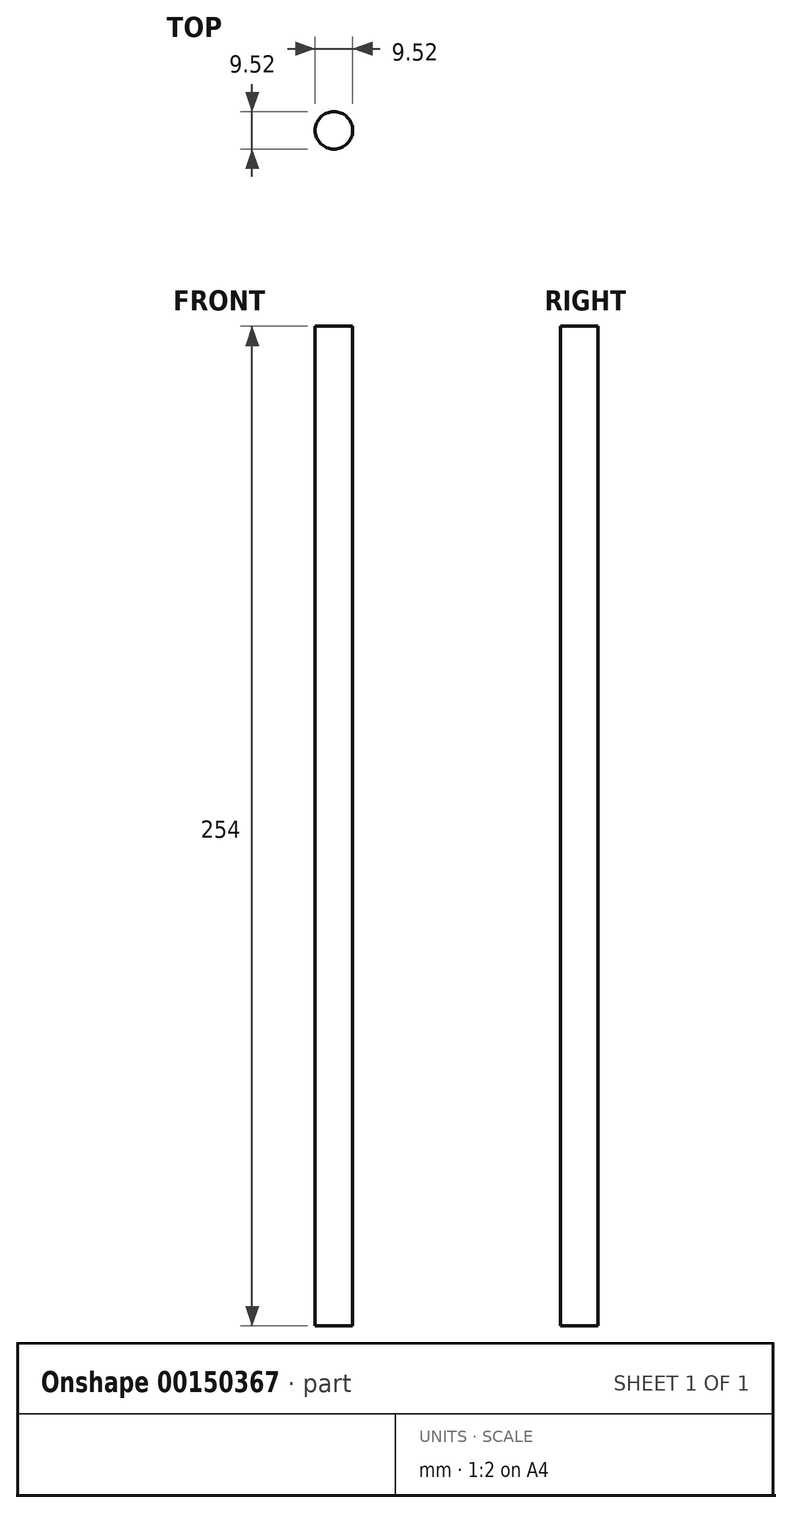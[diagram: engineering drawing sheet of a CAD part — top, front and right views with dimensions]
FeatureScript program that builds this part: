
annotation { "Feature Type Name" : "Feature", "Feature Type Description" : "" }
export const myFeature = defineFeature(function(context is Context, id is Id, definition is map)
    precondition{}
    {
        {
            var Q0;
            Q0=qCreatedBy(makeId("Top.planeOp"),FACE);
            var sketch = newSketch(context, id + "F0", { "sketchPlane" : qUnion([Q0])});
            skCircle(sketch, "E0", {"center": v(0, 0) * mm, "radius": 4.76 * mm});
            skSolve(sketch);
        }
        {
            var Q0;
            Q0 = qSketchRegion(id + "F0", true);
            extrude(context, id + "F1", {"entities" : qUnion([Q0]), "depth" : 254 * mm});
        }
    });
